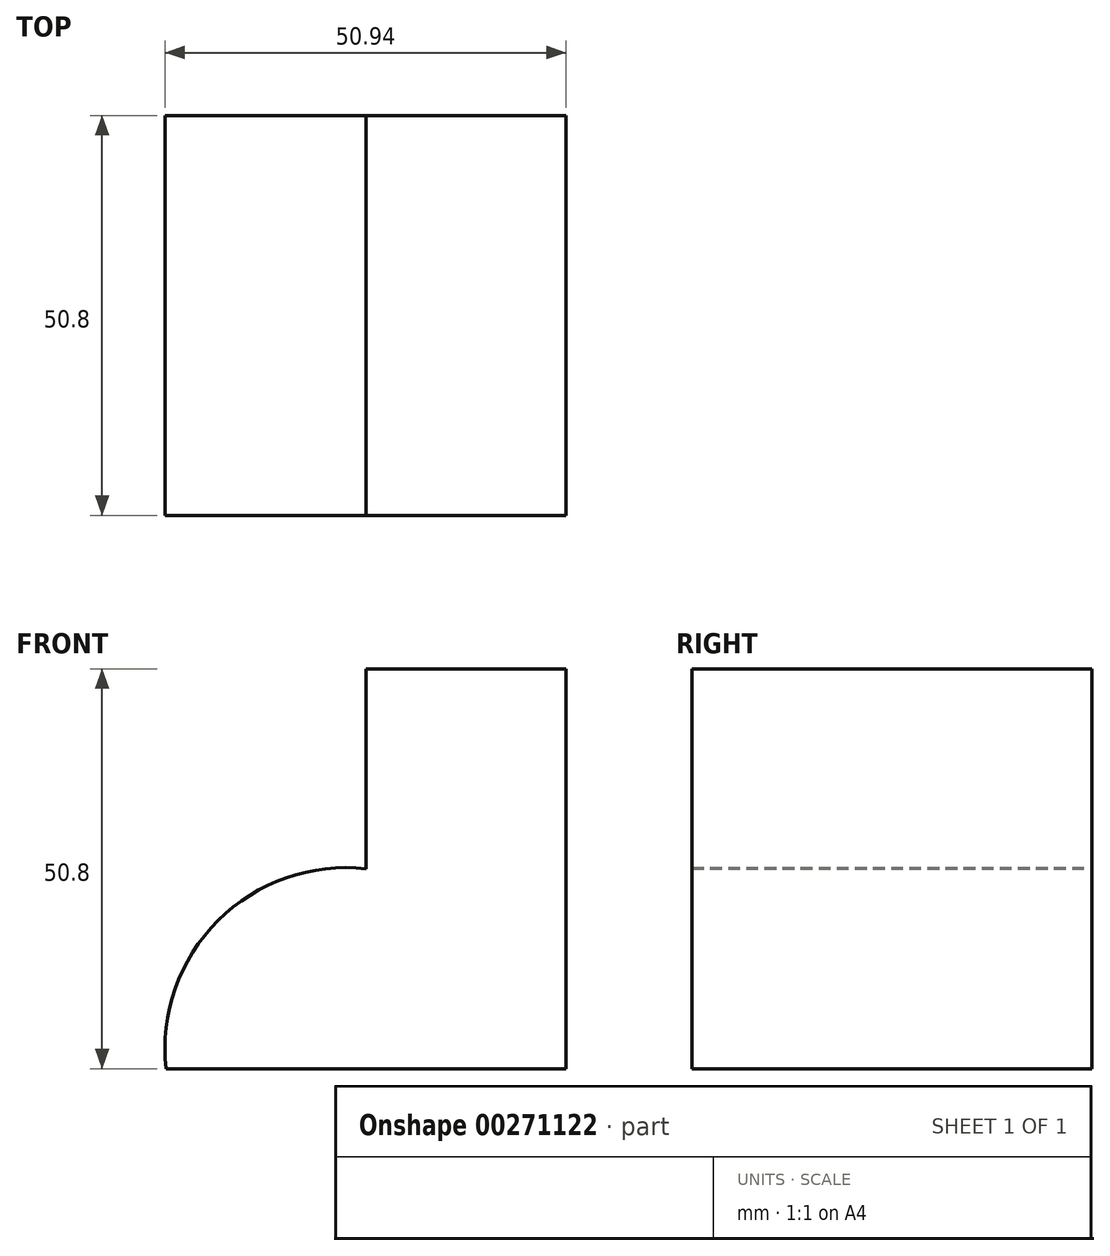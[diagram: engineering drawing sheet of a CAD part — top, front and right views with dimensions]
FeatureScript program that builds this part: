
annotation { "Feature Type Name" : "Feature", "Feature Type Description" : "" }
export const myFeature = defineFeature(function(context is Context, id is Id, definition is map)
    precondition{}
    {
        {
            var Q0;
            Q0=qCreatedBy(makeId("Front.planeOp"),FACE);
            var sketch = newSketch(context, id + "F0", { "sketchPlane" : qUnion([Q0])});
            skLineSegment(sketch, "E0", {"start": v(-50.8, 0) * mm, "end": v(0, 0) * mm});
            skLineSegment(sketch, "E1", {"start": v(0, 0) * mm, "end": v(0, 50.8) * mm});
            skLineSegment(sketch, "E2", {"start": v(0, 50.8) * mm, "end": v(-25.4, 50.8) * mm});
            skLineSegment(sketch, "E3", {"start": v(-25.4, 50.8) * mm, "end": v(-25.4, 25.4) * mm});
            skArc(sketch, "E4", {"start": v(-25.4, 25.4) * mm, "mid": v(-44.21, 18.81) * mm, "end": v(-50.8, 0) * mm});
            skSolve(sketch);
        }
        {
            var Q0;
            Q0=makeQuery(id+"F0.imprint","IMPRINT",FACE,{"disambiguationData":[TD([[makeQuery(id+"F0.imprint","IMPRINT",EDGE,{"derivedFrom":sQuery(id+"F0.wireOp",EDGE,"E0")}),1.0]])]});
            extrude(context, id + "F1", {"entities" : qUnion([Q0]), "depth" : 50.8 * mm});
        }
    });
